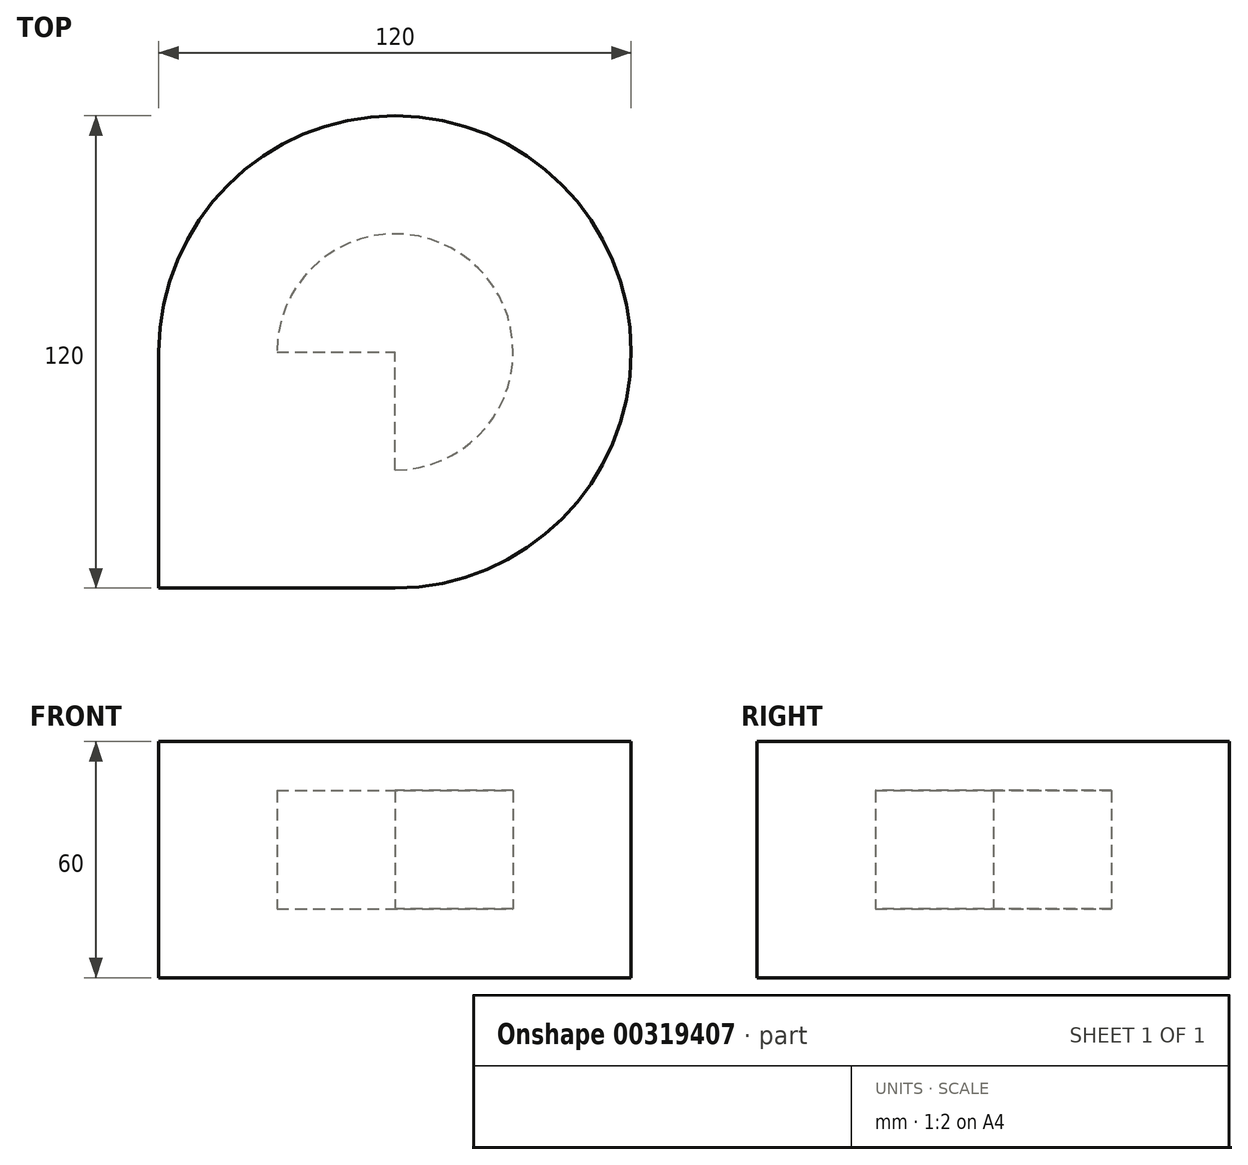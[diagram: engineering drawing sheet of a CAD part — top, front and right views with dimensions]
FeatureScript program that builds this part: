
annotation { "Feature Type Name" : "Feature", "Feature Type Description" : "" }
export const myFeature = defineFeature(function(context is Context, id is Id, definition is map)
    precondition{}
    {
        {
            var Q0;
            Q0=qCreatedBy(makeId("Front.planeOp"),FACE);
            var sketch = newSketch(context, id + "F0", { "sketchPlane" : qUnion([Q0])});
            skLineSegment(sketch, "E0.bottom", {"start": v(0, 0) * mm, "end": v(-60, 0) * mm});
            skLineSegment(sketch, "E0.top", {"start": v(0, -60) * mm, "end": v(-60, -60) * mm});
            skLineSegment(sketch, "E0.left", {"start": v(0, 0) * mm, "end": v(0, -60) * mm});
            skLineSegment(sketch, "E0.right", {"start": v(-60, 0) * mm, "end": v(-60, -60) * mm});
            skSolve(sketch);
        }
        {
            var Q0;
            Q0 = qSketchRegion(id + "F0", true);
            extrude(context, id + "F1", {"entities" : qUnion([Q0]), "depth" : 60 * mm});
        }
        {
            var Q0;
            Q0=makeQuery(id+"F1.opExtrude","CAP_FACE",FACE,{"disambiguationData":[OSD([sQuery(id+"F0.wireOp",EDGE,"E0.bottom"),sQuery(id+"F0.wireOp",EDGE,"E0.top"),sQuery(id+"F0.wireOp",EDGE,"E0.left"),sQuery(id+"F0.wireOp",EDGE,"E0.right")])],"isStart":true});
            var sketch = newSketch(context, id + "F2", { "sketchPlane" : qUnion([Q0])});
            skLineSegment(sketch, "E1.bottom", {"start": v(0, -42.47) * mm, "end": v(-30, -42.47) * mm});
            skLineSegment(sketch, "E1.top", {"start": v(0, -12.47) * mm, "end": v(-30, -12.47) * mm});
            skLineSegment(sketch, "E1.left", {"start": v(0, -42.47) * mm, "end": v(0, -12.47) * mm});
            skLineSegment(sketch, "E1.right", {"start": v(-30, -42.47) * mm, "end": v(-30, -12.47) * mm});
            skSolve(sketch);
        }
        {
            var Q0;
            Q0=makeQuery(id+"F2.imprint","IMPRINT",FACE,{"disambiguationData":[TD([[makeQuery(id+"F2.imprint","IMPRINT",EDGE,{"derivedFrom":sQuery(id+"F2.wireOp",EDGE,"E1.bottom")}),-1.0]])]});
            var Q1;
            {var subQ2=sQuery(id+"F2.wireOp",EDGE,"E1.left");Q1=makeQuery(id+"F2.imprint","IMPRINT",FACE,{"disambiguationData":[TD([[makeQuery(id+"F2.imprint","IMPRINT",EDGE,{"derivedFrom":subQ2}),1.0]])]});}
            var Q2;
            Q2=sQuery(id+"F2.wireOp",EDGE,"E1.left");
            revolve(context, id + "F3", {"operationType" : NewBodyOperationType.ADD, "entities" : qUnion([Q0, Q1]), "axis" : qUnion([Q2]), "revolveType" : RevolveType.FULL});
        }
    });
